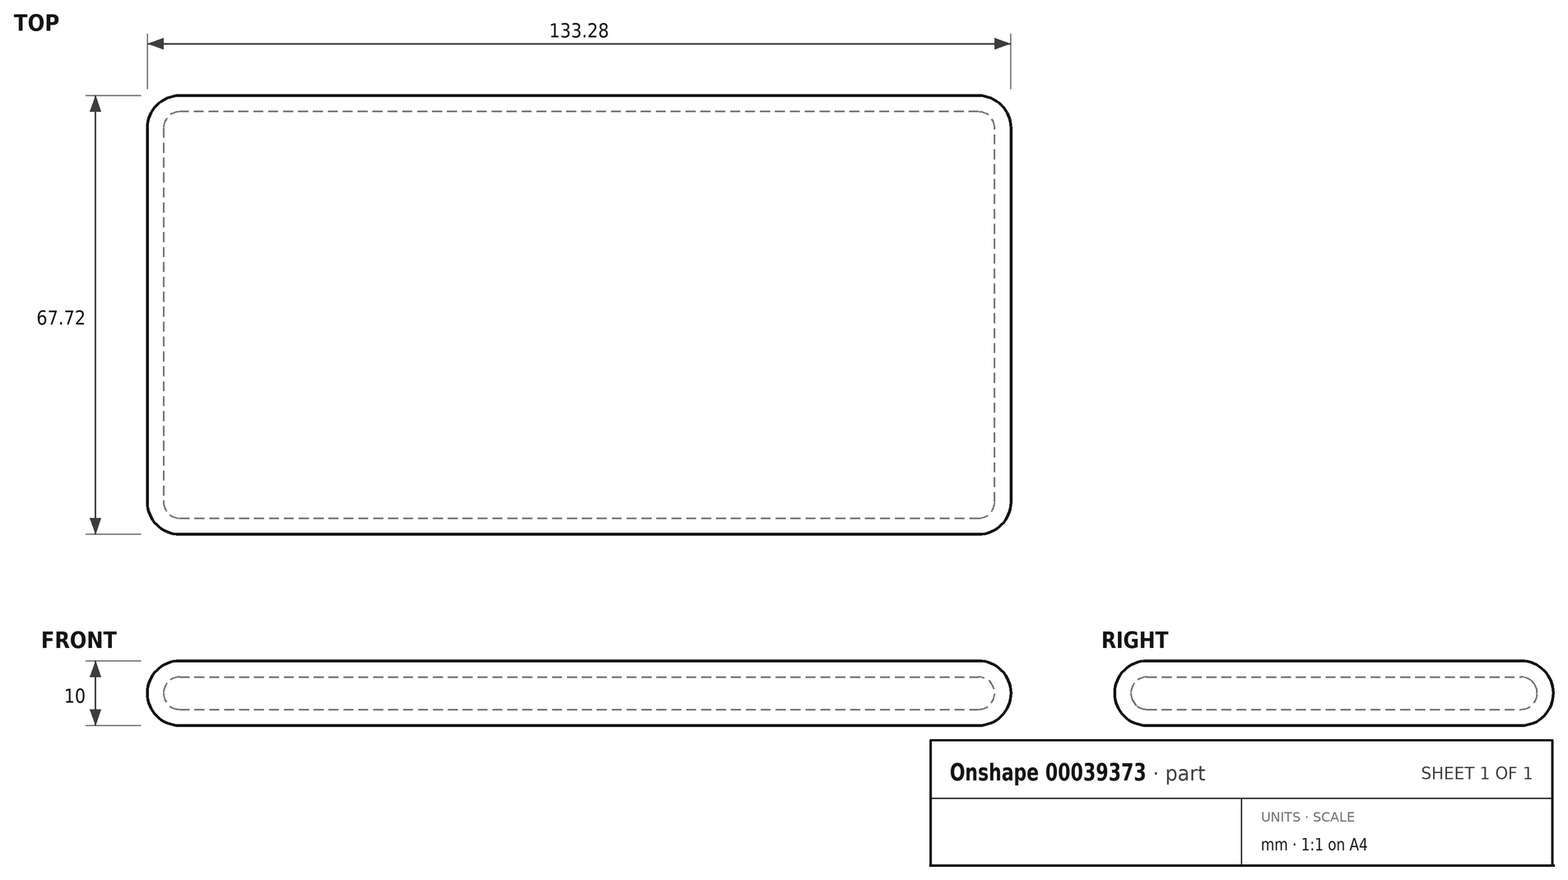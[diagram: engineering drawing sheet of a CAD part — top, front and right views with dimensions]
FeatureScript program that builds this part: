
annotation { "Feature Type Name" : "Feature", "Feature Type Description" : "" }
export const myFeature = defineFeature(function(context is Context, id is Id, definition is map)
    precondition{}
    {
        {
            var Q0;
            Q0=qCreatedBy(makeId("Top.planeOp"),FACE);
            var sketch = newSketch(context, id + "F0", { "sketchPlane" : qUnion([Q0])});
            skLineSegment(sketch, "E0.rect.bottom", {"start": v(-66.64, 33.86) * mm, "end": v(66.64, 33.86) * mm});
            skLineSegment(sketch, "E0.rect.top", {"start": v(-66.64, -33.86) * mm, "end": v(66.64, -33.86) * mm});
            skLineSegment(sketch, "E0.rect.left", {"start": v(-66.64, 33.86) * mm, "end": v(-66.64, -33.86) * mm});
            skLineSegment(sketch, "E0.rect.right", {"start": v(66.64, 33.86) * mm, "end": v(66.64, -33.86) * mm});
            skPoint(sketch, "E0.rect.middle", {"position": v(0, 0) * mm});
            skSolve(sketch);
        }
        {
            var Q0;
            Q0 = qSketchRegion(id + "F0", true);
            extrude(context, id + "F1", {"entities" : qUnion([Q0]), "depth" : 10 * mm});
        }
        {
            var Q0;
            Q0=makeQuery(id+"F1.opExtrude","SWEPT_FACE",FACE,{"disambiguationData":[OSD([sQuery(id+"F0.wireOp",EDGE,"E0.rect.bottom")])]});
            var Q1;
            Q1=makeQuery(id+"F1.opExtrude","SWEPT_FACE",FACE,{"disambiguationData":[OSD([sQuery(id+"F0.wireOp",EDGE,"E0.rect.left")])]});
            var Q2;
            Q2=makeQuery(id+"F1.opExtrude","SWEPT_FACE",FACE,{"disambiguationData":[OSD([sQuery(id+"F0.wireOp",EDGE,"E0.rect.top")])]});
            var Q3;
            Q3=makeQuery(id+"F1.opExtrude","SWEPT_FACE",FACE,{"disambiguationData":[OSD([sQuery(id+"F0.wireOp",EDGE,"E0.rect.right")])]});
            fillet(context, id + "F2", {"entities" : qUnion([Q0, Q1, Q2, Q3]), "radius" : 5 * mm, "tangentPropagation" : true, "allowEdgeOverflow" : false});
        }
        {
            var Q0;
            Q0=makeQuery(id+"F1.opExtrude","CAP_FACE",FACE,{"disambiguationData":[OSD([sQuery(id+"F0.wireOp",EDGE,"E0.rect.bottom"),sQuery(id+"F0.wireOp",EDGE,"E0.rect.top"),sQuery(id+"F0.wireOp",EDGE,"E0.rect.left"),sQuery(id+"F0.wireOp",EDGE,"E0.rect.right")])],"isStart":false});
            var Q1;
            Q1=makeQuery(id+"F2.opFillet","BLEND_FACE",FACE,{"disambiguationData":[OSD([sQuery(id+"F0.wireOp",EDGE,"E0.rect.bottom")])]});
            var Q2;
            Q2=makeQuery(id+"F1.opExtrude","SWEPT_BODY",BODY,{"disambiguationData":[OSD([sQuery(id+"F0.wireOp",EDGE,"E0.rect.bottom"),sQuery(id+"F0.wireOp",EDGE,"E0.rect.top"),sQuery(id+"F0.wireOp",EDGE,"E0.rect.left"),sQuery(id+"F0.wireOp",EDGE,"E0.rect.right")])]});
            shell(context, id + "F3", {"isHollow" : true, "entities" : qUnion([Q0, Q1]), "parts" : qUnion([Q2]), "thickness" : 2.5 * mm});
        }
    });
